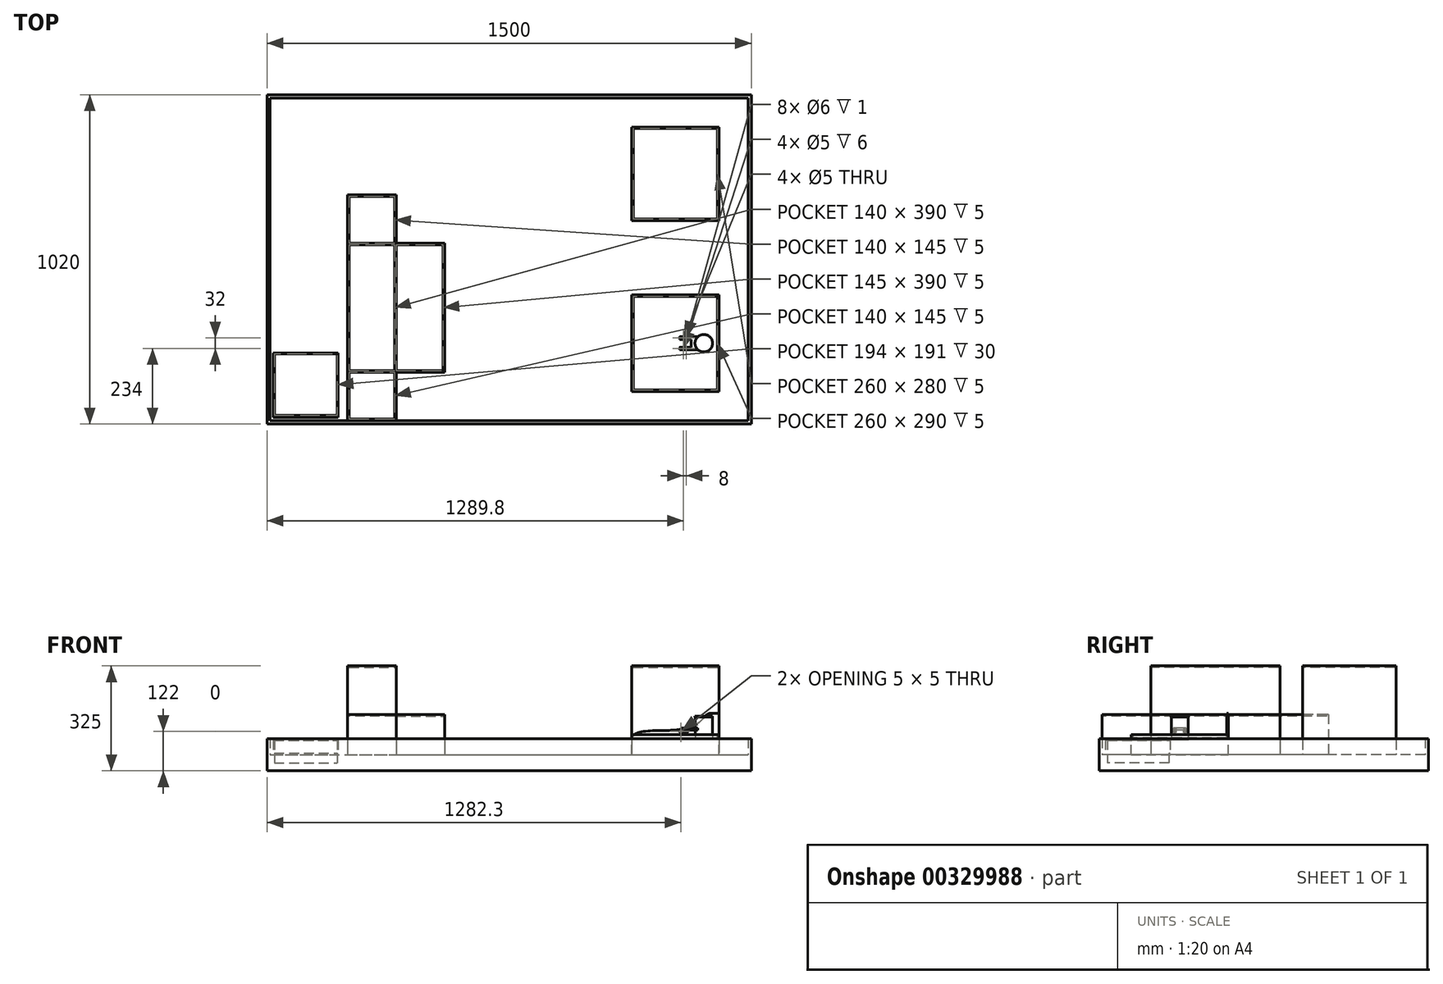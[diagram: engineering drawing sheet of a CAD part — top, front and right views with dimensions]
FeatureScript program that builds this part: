
annotation { "Feature Type Name" : "Feature", "Feature Type Description" : "" }
export const myFeature = defineFeature(function(context is Context, id is Id, definition is map)
    precondition{}
    {
        {
            var Q0;
            Q0=qCreatedBy(makeId("Top.planeOp"),FACE);
            var sketch = newSketch(context, id + "F0", { "sketchPlane" : qUnion([Q0])});
            skCircle(sketch, "E0", {"center": v(0, 0) * mm, "radius": 27.2 * mm});
            skSolve(sketch);
        }
        {
            var Q0;
            Q0=qSketchRegion(id+"F0",true);
            extrude(context, id + "F1", {"entities" : qUnion([Q0]), "depth" : 2.83 * mm});
        }
        {
            var Q0;
            Q0=makeQuery(id+"F1.opExtrude","CAP_FACE",FACE,{"disambiguationData":[OSD([sQuery(id+"F0.wireOp",EDGE,"E0")])],"isStart":false});
            var sketch = newSketch(context, id + "F2", { "sketchPlane" : qUnion([Q0])});
            skCircle(sketch, "E1", {"center": v(0, 0) * mm, "radius": 26.4 * mm});
            skSolve(sketch);
        }
        {
            var Q0;
            Q0=qSketchRegion(id+"F2",true);
            extrude(context, id + "F3", {"entities" : qUnion([Q0]), "operationType" : NewBodyOperationType.ADD, "depth" : 67.36 * mm});
        }
        {
            var Q0;
            Q0=makeQuery(id+"F3.opExtrude","CAP_FACE",FACE,{"disambiguationData":[OSD([sQuery(id+"F2.wireOp",EDGE,"E1")])],"isStart":false});
            var sketch = newSketch(context, id + "F4", { "sketchPlane" : qUnion([Q0])});
            skCircle(sketch, "E2", {"center": v(0, 0) * mm, "radius": 27.2 * mm});
            skSolve(sketch);
        }
        {
            var Q0;
            Q0=qSketchRegion(id+"F4",true);
            extrude(context, id + "F5", {"entities" : qUnion([Q0]), "operationType" : NewBodyOperationType.ADD, "depth" : 2.83 * mm});
        }
        {
            var Q0;
            Q0=makeQuery(id+"F5.opExtrude","CAP_FACE",FACE,{"disambiguationData":[OSD([sQuery(id+"F4.wireOp",EDGE,"E2")])],"isStart":false});
            var sketch = newSketch(context, id + "F6", { "sketchPlane" : qUnion([Q0])});
            skSolve(sketch);
        }
        {
            var Q0;
            Q0=qCreatedBy(makeId("Top.planeOp"),FACE);
            cPlane(context, id + "F7", {"entities" : qUnion([Q0]), "cplaneType" : CPlaneType.OFFSET, "offset" : 25 * mm, "width" : 150 * mm, "height" : 150 * mm});
        }
        {
            var Q0;
            Q0=makeQuery(id+"F6.imprint","IMPRINT",FACE,{"disambiguationData":[TD([[makeQuery(id+"F6.imprint","IMPRINT",EDGE,{"derivedFrom":makeQuery(id+"F5.opExtrude","CAP_EDGE",EDGE,{"disambiguationData":[OSD([sQuery(id+"F4.wireOp",EDGE,"E2")])],"isStart":false})}),1.0]])]});
            var sketch = newSketch(context, id + "F8", { "sketchPlane" : qUnion([Q0])});
            skSolve(sketch);
        }
        {
            var Q0;
            Q0=qCreatedBy(makeId("Top.planeOp"),FACE);
            var sketch = newSketch(context, id + "F9", { "sketchPlane" : qUnion([Q0])});
            skLineSegment(sketch, "E3.bottom", {"start": v(-222.8, -150) * mm, "end": v(47.2, -150) * mm});
            skLineSegment(sketch, "E3.top", {"start": v(-222.8, 150) * mm, "end": v(47.2, 150) * mm});
            skLineSegment(sketch, "E3.left", {"start": v(-222.8, -150) * mm, "end": v(-222.8, 150) * mm});
            skLineSegment(sketch, "E3.right", {"start": v(47.2, -150) * mm, "end": v(47.2, 150) * mm});
            skSolve(sketch);
        }
        {
            var Q0;
            Q0=qSketchRegion(id+"F9",true);
            extrude(context, id + "F10", {"entities" : qUnion([Q0]), "oppositeDirection" : true, "depth" : 72 * mm});
        }
        {
            var Q0;
            Q0=makeQuery(id+"F10.opExtrude","CAP_FACE",FACE,{"disambiguationData":[OSD([sQuery(id+"F9.wireOp",EDGE,"E3.bottom"),sQuery(id+"F9.wireOp",EDGE,"E3.top"),sQuery(id+"F9.wireOp",EDGE,"E3.left"),sQuery(id+"F9.wireOp",EDGE,"E3.right")])],"isStart":true});
            var sketch = newSketch(context, id + "F11", { "sketchPlane" : qUnion([Q0])});
            skLineSegment(sketch, "E4.bottom", {"start": v(-222.8, -150) * mm, "end": v(47.2, -150) * mm});
            skLineSegment(sketch, "E4.top", {"start": v(-222.8, -145) * mm, "end": v(42.2, -145) * mm});
            skLineSegment(sketch, "E4.left", {"start": v(-222.8, -150) * mm, "end": v(-222.8, -145) * mm});
            skLineSegment(sketch, "E5.bottom", {"start": v(47.2, 150) * mm, "end": v(42.2, 150) * mm});
            skLineSegment(sketch, "E5.left", {"start": v(47.2, 150) * mm, "end": v(47.2, -150) * mm});
            skLineSegment(sketch, "E5.right", {"start": v(42.2, 150) * mm, "end": v(42.2, -145) * mm});
            skSolve(sketch);
        }
        {
            var Q0;
            Q0=qSketchRegion(id+"F11",true);
            extrude(context, id + "F12", {"entities" : qUnion([Q0]), "operationType" : NewBodyOperationType.ADD, "depth" : 15 * mm});
        }
        {
            var Q0;
            Q0=makeQuery(id+"F12.boolean.opBoolean","MERGE",FACE,{"derivedFrom":[makeQuery(id+"F10.opExtrude","SWEPT_FACE",FACE,{"disambiguationData":[OSD([sQuery(id+"F9.wireOp",EDGE,"E3.top")])]}),makeQuery(id+"F12.opExtrude","SWEPT_FACE",FACE,{"disambiguationData":[OSD([sQuery(id+"F11.wireOp",EDGE,"E5.bottom")])]})]});
            var sketch = newSketch(context, id + "F13", { "sketchPlane" : qUnion([Q0])});
            skLineSegment(sketch, "E6", {"start": v(-47.2, 81.36) * mm, "end": v(-21.31, 81.36) * mm});
            skFitSpline(sketch, "E7", {"points": [v(-21.31, 81.36) * mm, v(15.24, 52.01) * mm, v(114.14, 28.17) * mm, v(222.8, 0) * mm], "startDerivative": vector(181.02, 0.3) * mm, "endDerivative": vector(-1.73, -239.85) * mm});
            skLineSegment(sketch, "E8", {"start": v(-47.2, 81.36) * mm, "end": v(-47.2, -72) * mm});
            skLineSegment(sketch, "E9", {"start": v(-47.2, -72) * mm, "end": v(222.8, -72) * mm});
            skLineSegment(sketch, "E10", {"start": v(222.8, -72) * mm, "end": v(222.8, 0) * mm});
            skSolve(sketch);
        }
        {
            var Q0;
            Q0=qSketchRegion(id+"F13",true);
            extrude(context, id + "F14", {"entities" : qUnion([Q0]), "operationType" : NewBodyOperationType.ADD, "oppositeDirection" : true, "depth" : 5 * mm});
        }
        {
            var Q0;
            Q0=makeQuery(id+"F10.opExtrude","CAP_FACE",FACE,{"disambiguationData":[OSD([sQuery(id+"F9.wireOp",EDGE,"E3.bottom"),sQuery(id+"F9.wireOp",EDGE,"E3.top"),sQuery(id+"F9.wireOp",EDGE,"E3.left"),sQuery(id+"F9.wireOp",EDGE,"E3.right")])],"isStart":true});
            var sketch = newSketch(context, id + "F15", { "sketchPlane" : qUnion([Q0])});
            skLineSegment(sketch, "E11.bottom", {"start": v(-222.8, 145) * mm, "end": v(-217.8, 145) * mm});
            skLineSegment(sketch, "E11.top", {"start": v(-222.8, -145) * mm, "end": v(-217.8, -145) * mm});
            skLineSegment(sketch, "E11.left", {"start": v(-222.8, 145) * mm, "end": v(-222.8, -145) * mm});
            skLineSegment(sketch, "E11.right", {"start": v(-217.8, 145) * mm, "end": v(-217.8, -145) * mm});
            skSolve(sketch);
        }
        {
            var Q0;
            Q0=qSketchRegion(id+"F15",true);
            extrude(context, id + "F16", {"entities" : qUnion([Q0]), "operationType" : NewBodyOperationType.ADD, "depth" : 5 * mm});
        }
        {
            var Q0;
            Q0=makeQuery(id+"F10.opExtrude","CAP_FACE",FACE,{"disambiguationData":[OSD([sQuery(id+"F9.wireOp",EDGE,"E3.bottom"),sQuery(id+"F9.wireOp",EDGE,"E3.top"),sQuery(id+"F9.wireOp",EDGE,"E3.left"),sQuery(id+"F9.wireOp",EDGE,"E3.right")])],"isStart":false});
            var sketch = newSketch(context, id + "F17", { "sketchPlane" : qUnion([Q0])});
            skLineSegment(sketch, "E12.bottom", {"start": v(147.2, 250) * mm, "end": v(-1352.8, 250) * mm});
            skLineSegment(sketch, "E12.top", {"start": v(147.2, -770) * mm, "end": v(-1352.8, -770) * mm});
            skLineSegment(sketch, "E12.left", {"start": v(147.2, 250) * mm, "end": v(147.2, -770) * mm});
            skLineSegment(sketch, "E12.right", {"start": v(-1352.8, 250) * mm, "end": v(-1352.8, -770) * mm});
            skSolve(sketch);
        }
        {
            var Q0;
            Q0=qSketchRegion(id+"F17",true);
            extrude(context, id + "F18", {"entities" : qUnion([Q0]), "operationType" : NewBodyOperationType.ADD, "depth" : 25 * mm});
        }
        {
            var Q0;
            Q0=makeQuery(id+"F18.opExtrude","CAP_FACE",FACE,{"disambiguationData":[OSD([sQuery(id+"F17.wireOp",EDGE,"E12.bottom"),sQuery(id+"F17.wireOp",EDGE,"E12.top"),sQuery(id+"F17.wireOp",EDGE,"E12.left"),sQuery(id+"F17.wireOp",EDGE,"E12.right")])],"isStart":true});
            var sketch = newSketch(context, id + "F19", { "sketchPlane" : qUnion([Q0])});
            skLineSegment(sketch, "E13.bottom", {"start": v(-222.8, 670) * mm, "end": v(47.2, 670) * mm});
            skLineSegment(sketch, "E13.top", {"start": v(-222.8, 380) * mm, "end": v(47.2, 380) * mm});
            skLineSegment(sketch, "E13.left", {"start": v(-222.8, 670) * mm, "end": v(-222.8, 380) * mm});
            skLineSegment(sketch, "E13.right", {"start": v(47.2, 670) * mm, "end": v(47.2, 380) * mm});
            skSolve(sketch);
        }
        {
            var Q0;
            Q0=qSketchRegion(id+"F19",true);
            extrude(context, id + "F20", {"entities" : qUnion([Q0]), "operationType" : NewBodyOperationType.ADD, "depth" : 300 * mm});
        }
        {
            var Q0;
            Q0=makeQuery(id+"F20.opExtrude","CAP_FACE",FACE,{"disambiguationData":[OSD([sQuery(id+"F19.wireOp",EDGE,"E13.bottom"),sQuery(id+"F19.wireOp",EDGE,"E13.top"),sQuery(id+"F19.wireOp",EDGE,"E13.left"),sQuery(id+"F19.wireOp",EDGE,"E13.right")])],"isStart":false});
            var sketch = newSketch(context, id + "F21", { "sketchPlane" : qUnion([Q0])});
            skLineSegment(sketch, "E14.bottom", {"start": v(-217.8, 665) * mm, "end": v(42.2, 665) * mm});
            skLineSegment(sketch, "E14.top", {"start": v(-217.8, 385) * mm, "end": v(42.2, 385) * mm});
            skLineSegment(sketch, "E14.left", {"start": v(-217.8, 665) * mm, "end": v(-217.8, 385) * mm});
            skLineSegment(sketch, "E14.right", {"start": v(42.2, 665) * mm, "end": v(42.2, 385) * mm});
            skSolve(sketch);
        }
        {
            var Q0;
            Q0=qSketchRegion(id+"F21",true);
            extrude(context, id + "F22", {"entities" : qUnion([Q0]), "operationType" : NewBodyOperationType.REMOVE, "oppositeDirection" : true, "depth" : 5 * mm});
        }
        {
            var Q0;
            Q0=makeQuery(id+"F18.opExtrude","CAP_FACE",FACE,{"disambiguationData":[OSD([sQuery(id+"F17.wireOp",EDGE,"E12.bottom"),sQuery(id+"F17.wireOp",EDGE,"E12.top"),sQuery(id+"F17.wireOp",EDGE,"E12.left"),sQuery(id+"F17.wireOp",EDGE,"E12.right")])],"isStart":true});
            var sketch = newSketch(context, id + "F23", { "sketchPlane" : qUnion([Q0])});
            skLineSegment(sketch, "E15.bottom", {"start": v(-1352.8, 770) * mm, "end": v(147.2, 770) * mm});
            skLineSegment(sketch, "E15.top", {"start": v(-1352.8, -250) * mm, "end": v(147.2, -250) * mm});
            skLineSegment(sketch, "E15.left", {"start": v(-1352.8, 770) * mm, "end": v(-1352.8, -250) * mm});
            skLineSegment(sketch, "E15.right", {"start": v(147.2, 770) * mm, "end": v(147.2, -250) * mm});
            skLineSegment(sketch, "E16.bottom", {"start": v(-1342.8, 760) * mm, "end": v(137.2, 760) * mm});
            skLineSegment(sketch, "E16.top", {"start": v(-1342.8, -240) * mm, "end": v(137.2, -240) * mm});
            skLineSegment(sketch, "E16.left", {"start": v(-1342.8, 760) * mm, "end": v(-1342.8, -240) * mm});
            skLineSegment(sketch, "E16.right", {"start": v(137.2, 760) * mm, "end": v(137.2, -240) * mm});
            skSolve(sketch);
        }
        {
            var Q0;
            Q0=qSketchRegion(id+"F23",true);
            extrude(context, id + "F24", {"entities" : qUnion([Q0]), "operationType" : NewBodyOperationType.ADD, "depth" : 75 * mm});
        }
        {
            var Q0;
            Q0=makeQuery(id+"F18.opExtrude","CAP_FACE",FACE,{"disambiguationData":[OSD([sQuery(id+"F17.wireOp",EDGE,"E12.bottom"),sQuery(id+"F17.wireOp",EDGE,"E12.top"),sQuery(id+"F17.wireOp",EDGE,"E12.left"),sQuery(id+"F17.wireOp",EDGE,"E12.right")])],"isStart":true});
            var sketch = newSketch(context, id + "F25", { "sketchPlane" : qUnion([Q0])});
            skLineSegment(sketch, "E17.bottom", {"start": v(-1102.8, 460) * mm, "end": v(-952.8, 460) * mm});
            skLineSegment(sketch, "E17.top", {"start": v(-1102.8, -240) * mm, "end": v(-952.8, -240) * mm});
            skLineSegment(sketch, "E17.left", {"start": v(-1102.8, 460) * mm, "end": v(-1102.8, -240) * mm});
            skLineSegment(sketch, "E17.right", {"start": v(-952.8, 460) * mm, "end": v(-952.8, 310) * mm});
            skLineSegment(sketch, "E18.bottom", {"start": v(-952.8, 310) * mm, "end": v(-802.8, 310) * mm});
            skLineSegment(sketch, "E18.top", {"start": v(-952.8, -90) * mm, "end": v(-802.8, -90) * mm});
            skLineSegment(sketch, "E18.right", {"start": v(-802.8, 310) * mm, "end": v(-802.8, -90) * mm});
            skLineSegment(sketch, "E19.trimOffspring", {"start": v(-952.8, -90) * mm, "end": v(-952.8, -240) * mm});
            skSolve(sketch);
        }
        {
            var Q0;
            Q0=qSketchRegion(id+"F25",true);
            extrude(context, id + "F26", {"entities" : qUnion([Q0]), "operationType" : NewBodyOperationType.ADD, "depth" : 150 * mm});
        }
        {
            var Q0;
            Q0=makeQuery(id+"F26.opExtrude","CAP_FACE",FACE,{"disambiguationData":[OSD([sQuery(id+"F25.wireOp",EDGE,"E17.bottom"),sQuery(id+"F25.wireOp",EDGE,"E17.top"),sQuery(id+"F25.wireOp",EDGE,"E17.left"),sQuery(id+"F25.wireOp",EDGE,"E17.right"),sQuery(id+"F25.wireOp",EDGE,"E18.bottom"),sQuery(id+"F25.wireOp",EDGE,"E18.top"),sQuery(id+"F25.wireOp",EDGE,"E18.right"),sQuery(id+"F25.wireOp",EDGE,"E19.trimOffspring")])],"isStart":false});
            var sketch = newSketch(context, id + "F27", { "sketchPlane" : qUnion([Q0])});
            skLineSegment(sketch, "E20.bottom", {"start": v(-952.8, 310) * mm, "end": v(-1102.8, 310) * mm});
            skLineSegment(sketch, "E20.top", {"start": v(-952.8, -90) * mm, "end": v(-1102.8, -90) * mm});
            skLineSegment(sketch, "E20.left", {"start": v(-952.8, 310) * mm, "end": v(-952.8, -90) * mm});
            skLineSegment(sketch, "E20.right", {"start": v(-1102.8, 310) * mm, "end": v(-1102.8, -90) * mm});
            skSolve(sketch);
        }
        {
            var Q0;
            Q0=qSketchRegion(id+"F27",true);
            extrude(context, id + "F28", {"entities" : qUnion([Q0]), "operationType" : NewBodyOperationType.ADD, "depth" : 150 * mm});
        }
        {
            var Q0;
            Q0=makeQuery(id+"F28.opExtrude","CAP_FACE",FACE,{"disambiguationData":[OSD([sQuery(id+"F27.wireOp",EDGE,"E20.bottom"),sQuery(id+"F27.wireOp",EDGE,"E20.top"),sQuery(id+"F27.wireOp",EDGE,"E20.left"),sQuery(id+"F27.wireOp",EDGE,"E20.right")])],"isStart":false});
            var sketch = newSketch(context, id + "F29", { "sketchPlane" : qUnion([Q0])});
            skLineSegment(sketch, "E21.bottom", {"start": v(-1097.8, 305) * mm, "end": v(-957.8, 305) * mm});
            skLineSegment(sketch, "E21.top", {"start": v(-1097.8, -85) * mm, "end": v(-957.8, -85) * mm});
            skLineSegment(sketch, "E21.left", {"start": v(-1097.8, 305) * mm, "end": v(-1097.8, -85) * mm});
            skLineSegment(sketch, "E21.right", {"start": v(-957.8, 305) * mm, "end": v(-957.8, -85) * mm});
            skSolve(sketch);
        }
        {
            var Q0;
            Q0=qSketchRegion(id+"F29",true);
            extrude(context, id + "F30", {"entities" : qUnion([Q0]), "operationType" : NewBodyOperationType.REMOVE, "oppositeDirection" : true, "depth" : 5 * mm});
        }
        {
            var Q0;
            {var subQ0=sQuery(id+"F25.wireOp",EDGE,"E17.left");var subQ1=sQuery(id+"F25.wireOp",EDGE,"E18.bottom");var subQ2=sQuery(id+"F25.wireOp",EDGE,"E17.right");var subQ3=sQuery(id+"F25.wireOp",EDGE,"E17.bottom");var subQ4=makeQuery(id+"F26.opExtrude","CAP_FACE",FACE,{"disambiguationData":[OSD([subQ3,sQuery(id+"F25.wireOp",EDGE,"E17.top"),subQ0,subQ2,subQ1,sQuery(id+"F25.wireOp",EDGE,"E18.top"),sQuery(id+"F25.wireOp",EDGE,"E18.right"),sQuery(id+"F25.wireOp",EDGE,"E19.trimOffspring")])],"isStart":false});Q0=makeQuery(id+"F28.boolean.opBoolean","SPLIT",FACE,{"disambiguationData":[TD([makeQuery(id+"F26.opExtrude","SWEPT_FACE",FACE,{"disambiguationData":[OSD([subQ3])]})])],"derivedFrom":subQ4});}
            var sketch = newSketch(context, id + "F31", { "sketchPlane" : qUnion([Q0])});
            skLineSegment(sketch, "E22.bottom", {"start": v(-1097.8, 455) * mm, "end": v(-957.8, 455) * mm});
            skLineSegment(sketch, "E22.top", {"start": v(-1097.8, 310) * mm, "end": v(-957.8, 310) * mm});
            skLineSegment(sketch, "E22.left", {"start": v(-1097.8, 455) * mm, "end": v(-1097.8, 310) * mm});
            skLineSegment(sketch, "E22.right", {"start": v(-957.8, 455) * mm, "end": v(-957.8, 310) * mm});
            skLineSegment(sketch, "E23.bottom", {"start": v(-952.8, 305) * mm, "end": v(-807.8, 305) * mm});
            skLineSegment(sketch, "E23.top", {"start": v(-952.8, -85) * mm, "end": v(-807.8, -85) * mm});
            skLineSegment(sketch, "E23.left", {"start": v(-952.8, 305) * mm, "end": v(-952.8, -85) * mm});
            skLineSegment(sketch, "E23.right", {"start": v(-807.8, 305) * mm, "end": v(-807.8, -85) * mm});
            skLineSegment(sketch, "E24.bottom", {"start": v(-1097.8, -90) * mm, "end": v(-957.8, -90) * mm});
            skLineSegment(sketch, "E24.top", {"start": v(-1097.8, -235) * mm, "end": v(-957.8, -235) * mm});
            skLineSegment(sketch, "E24.left", {"start": v(-1097.8, -90) * mm, "end": v(-1097.8, -235) * mm});
            skLineSegment(sketch, "E24.right", {"start": v(-957.8, -90) * mm, "end": v(-957.8, -235) * mm});
            skSolve(sketch);
        }
        {
            var Q0;
            Q0=qSketchRegion(id+"F31",true);
            extrude(context, id + "F32", {"entities" : qUnion([Q0]), "operationType" : NewBodyOperationType.REMOVE, "oppositeDirection" : true, "depth" : 5 * mm});
        }
        {
            var Q0;
            Q0=qCreatedBy(id+"F7.planeOp",FACE);
            var sketch = newSketch(context, id + "F33", { "sketchPlane" : qUnion([Q0])});
            skLineSegment(sketch, "E25", {"start": v(0, 0) * mm, "end": v(-90, 0) * mm, "construction": true});
            skLineSegment(sketch, "E26.bottom", {"start": v(-74.5, -12) * mm, "end": v(-55, -12) * mm});
            skLineSegment(sketch, "E26.top", {"start": v(-74.5, -20) * mm, "end": v(-55, -20) * mm});
            skLineSegment(sketch, "E26.left", {"start": v(-74.5, -12) * mm, "end": v(-74.5, -13) * mm});
            skPoint(sketch, "E27.visualSharp", {"position": v(-51, -12) * mm});
            skPoint(sketch, "E28.visualSharp", {"position": v(-51, -20) * mm});
            skCircle(sketch, "E29", {"center": v(-55, -16) * mm, "radius": 3 * mm});
            skLineSegment(sketch, "E30", {"start": v(-59, -3.98) * mm, "end": v(-59, -18.08) * mm, "construction": true});
            skCircle(sketch, "E31.MirrorC", {"center": v(-63, -16) * mm, "radius": 3 * mm});
            skLineSegment(sketch, "E32.bottom", {"start": v(-74.5, -13) * mm, "end": v(-65.65, -13) * mm});
            skLineSegment(sketch, "E32.top", {"start": v(-74.5, -19) * mm, "end": v(-65.65, -19) * mm});
            skArc(sketch, "E33", {"start": v(-65.65, -13) * mm, "mid": v(-67, -16) * mm, "end": v(-65.65, -19) * mm});
            skLineSegment(sketch, "E34.trimOffspring", {"start": v(-74.5, -19) * mm, "end": v(-74.5, -20) * mm});
            skArc(sketch, "E35.trimOffspring", {"start": v(-55, -20) * mm, "mid": v(-51, -16) * mm, "end": v(-55, -12) * mm});
            skLineSegment(sketch, "E36.MirrorCS", {"start": v(-74.5, 12) * mm, "end": v(-74.5, 13) * mm});
            skLineSegment(sketch, "E37.MirrorCS", {"start": v(-74.5, 19) * mm, "end": v(-74.5, 20) * mm});
            skPoint(sketch, "E38.MirrorP", {"position": v(-51, 12) * mm});
            skLineSegment(sketch, "E39.MirrorCS", {"start": v(-74.5, 12) * mm, "end": v(-55, 12) * mm});
            skPoint(sketch, "E40.MirrorP", {"position": v(-51, 20) * mm});
            skArc(sketch, "E41.MirrorCS", {"start": v(-65.65, 13) * mm, "mid": v(-67, 16) * mm, "end": v(-65.65, 19) * mm});
            skArc(sketch, "E42.MirrorCS", {"start": v(-55, 20) * mm, "mid": v(-51, 16) * mm, "end": v(-55, 12) * mm});
            skLineSegment(sketch, "E43.MirrorCS", {"start": v(-74.5, 20) * mm, "end": v(-55, 20) * mm});
            skCircle(sketch, "E44.MirrorC", {"center": v(-55, 16) * mm, "radius": 3 * mm});
            skCircle(sketch, "E45.MirrorC", {"center": v(-63, 16) * mm, "radius": 3 * mm});
            skLineSegment(sketch, "E46.MirrorCS", {"start": v(-74.5, 19) * mm, "end": v(-65.65, 19) * mm});
            skLineSegment(sketch, "E47.MirrorCS", {"start": v(-74.5, 13) * mm, "end": v(-65.65, 13) * mm});
            skSolve(sketch);
        }
        {
            var Q0;
            Q0=qSketchRegion(id+"F33",true);
            var Q1;
            Q1=qSketchRegion(id+"F36",true);
            extrude(context, id + "F34", {"entities" : qUnion([Q0, Q1]), "endBound" : BoundingType.SYMMETRIC, "depth" : 8 * mm});
        }
        {
            var Q0;
            Q0=makeQuery(id+"F34.opExtrude","CAP_EDGE",EDGE,{"disambiguationData":[OSD([sQuery(id+"F33.wireOp",EDGE,"E34.trimOffspring")])],"isStart":false});
            var Q1;
            Q1=makeQuery(id+"F34.opExtrude","CAP_EDGE",EDGE,{"disambiguationData":[OSD([sQuery(id+"F33.wireOp",EDGE,"E26.left")])],"isStart":false});
            var Q2;
            Q2=makeQuery(id+"F34.opExtrude","CAP_EDGE",EDGE,{"disambiguationData":[OSD([sQuery(id+"F33.wireOp",EDGE,"E34.trimOffspring")])],"isStart":true});
            var Q3;
            Q3=makeQuery(id+"F34.opExtrude","CAP_EDGE",EDGE,{"disambiguationData":[OSD([sQuery(id+"F33.wireOp",EDGE,"E26.left")])],"isStart":true});
            var Q4;
            Q4=makeQuery(id+"F34.opExtrude","CAP_EDGE",EDGE,{"disambiguationData":[OSD([sQuery(id+"F33.wireOp",EDGE,"E36.MirrorCS")])],"isStart":false});
            var Q5;
            Q5=makeQuery(id+"F34.opExtrude","CAP_EDGE",EDGE,{"disambiguationData":[OSD([sQuery(id+"F33.wireOp",EDGE,"E37.MirrorCS")])],"isStart":false});
            var Q6;
            Q6=makeQuery(id+"F34.opExtrude","CAP_EDGE",EDGE,{"disambiguationData":[OSD([sQuery(id+"F33.wireOp",EDGE,"E37.MirrorCS")])],"isStart":true});
            var Q7;
            Q7=makeQuery(id+"F34.opExtrude","CAP_EDGE",EDGE,{"disambiguationData":[OSD([sQuery(id+"F33.wireOp",EDGE,"E36.MirrorCS")])],"isStart":true});
            fillet(context, id + "F35", {"entities" : qUnion([Q0, Q1, Q2, Q3, Q4, Q5, Q6, Q7]), "radius" : 4 * mm, "tangentPropagation" : true, "allowEdgeOverflow" : false});
        }
        {
            var Q0;
            Q0=makeQuery(id+"F34.opExtrude","SWEPT_FACE",FACE,{"disambiguationData":[OSD([sQuery(id+"F33.wireOp",EDGE,"E26.top")])]});
            var sketch = newSketch(context, id + "F36", { "sketchPlane" : qUnion([Q0])});
            skCircle(sketch, "E48", {"center": v(-70.5, 25) * mm, "radius": 3 * mm});
            skSolve(sketch);
        }
        {
            var Q0;
            Q0=qSketchRegion(id+"F36",true);
            var Q1;
            Q1=makeQuery(id+"F34.opExtrude","SWEPT_FACE",FACE,{"disambiguationData":[OSD([sQuery(id+"F33.wireOp",EDGE,"E26.bottom")])]});
            extrude(context, id + "F37", {"entities" : qUnion([Q0]), "operationType" : NewBodyOperationType.ADD, "endBound" : BoundingType.UP_TO_SURFACE, "oppositeDirection" : true, "endBoundEntityFace" : qUnion([Q1]), "depth" : 25 * mm});
        }
        {
            var Q0;
            Q0=makeQuery(id+"F34.opExtrude","SWEPT_FACE",FACE,{"disambiguationData":[OSD([sQuery(id+"F33.wireOp",EDGE,"E43.MirrorCS")])]});
            var sketch = newSketch(context, id + "F38", { "sketchPlane" : qUnion([Q0])});
            skCircle(sketch, "E49", {"center": v(70.5, 25) * mm, "radius": 3 * mm});
            skSolve(sketch);
        }
        {
            var Q0;
            Q0=qSketchRegion(id+"F38",true);
            var Q1;
            Q1=makeQuery(id+"F34.opExtrude","SWEPT_FACE",FACE,{"disambiguationData":[OSD([sQuery(id+"F33.wireOp",EDGE,"E39.MirrorCS")])]});
            extrude(context, id + "F39", {"entities" : qUnion([Q0]), "operationType" : NewBodyOperationType.ADD, "endBound" : BoundingType.UP_TO_SURFACE, "oppositeDirection" : true, "endBoundEntityFace" : qUnion([Q1]), "depth" : 25 * mm});
        }
        {
            var Q0;
            Q0=qCreatedBy(id+"F7.planeOp",FACE);
            var sketch = newSketch(context, id + "F40", { "sketchPlane" : qUnion([Q0])});
            skCircle(sketch, "E50", {"center": v(-55, 16) * mm, "radius": 3 * mm});
            skCircle(sketch, "E51", {"center": v(-63, 16) * mm, "radius": 2.5 * mm});
            skCircle(sketch, "E52", {"center": v(-63, 16) * mm, "radius": 3 * mm});
            skCircle(sketch, "E53", {"center": v(-55, 16) * mm, "radius": 2.5 * mm});
            skSolve(sketch);
        }
        {
            var Q0;
            Q0=qSketchRegion(id+"F40",true);
            extrude(context, id + "F41", {"entities" : qUnion([Q0]), "operationType" : NewBodyOperationType.ADD, "endBound" : BoundingType.SYMMETRIC, "depth" : 6 * mm});
        }
        {
            var Q0;
            Q0=qCreatedBy(id+"F7.planeOp",FACE);
            var sketch = newSketch(context, id + "F42", { "sketchPlane" : qUnion([Q0])});
            skCircle(sketch, "E54", {"center": v(-63, -16) * mm, "radius": 2.5 * mm});
            skCircle(sketch, "E55", {"center": v(-63, -16) * mm, "radius": 3 * mm});
            skCircle(sketch, "E56", {"center": v(-55, -16) * mm, "radius": 2.5 * mm});
            skCircle(sketch, "E57", {"center": v(-55, -16) * mm, "radius": 3 * mm});
            skSolve(sketch);
        }
        {
            var Q0;
            Q0=qSketchRegion(id+"F42",true);
            extrude(context, id + "F43", {"entities" : qUnion([Q0]), "operationType" : NewBodyOperationType.ADD, "endBound" : BoundingType.SYMMETRIC, "depth" : 6 * mm});
        }
        {
            var Q0;
            Q0=makeQuery(id+"F34.opExtrude","SWEPT_FACE",FACE,{"disambiguationData":[OSD([sQuery(id+"F33.wireOp",EDGE,"E43.MirrorCS")])]});
            var sketch = newSketch(context, id + "F44", { "sketchPlane" : qUnion([Q0])});
            skArc(sketch, "E58", {"start": v(71.5, 27.3) * mm, "mid": v(70.5, 27.5) * mm, "end": v(69.5, 27.3) * mm});
            skLineSegment(sketch, "E59.bottom", {"start": v(68.2, 26) * mm, "end": v(69.5, 26) * mm});
            skLineSegment(sketch, "E59.top", {"start": v(68.2, 24) * mm, "end": v(69.5, 24) * mm});
            skLineSegment(sketch, "E60.left", {"start": v(71.5, 27.3) * mm, "end": v(71.5, 26) * mm});
            skLineSegment(sketch, "E60.right", {"start": v(69.5, 27.3) * mm, "end": v(69.5, 26) * mm});
            skPoint(sketch, "E61.orphan", {"position": v(69.5, 27.8) * mm});
            skPoint(sketch, "E62.orphan", {"position": v(71.5, 27.8) * mm});
            skArc(sketch, "E63.trimOffspring", {"start": v(68.2, 26) * mm, "mid": v(68, 25) * mm, "end": v(68.2, 24) * mm});
            skPoint(sketch, "E59.left.start.orphan", {"position": v(67.32, 26) * mm});
            skPoint(sketch, "E64.orphan", {"position": v(67.32, 24) * mm});
            skArc(sketch, "E65.trimOffspring", {"start": v(69.5, 22.7) * mm, "mid": v(70.5, 22.5) * mm, "end": v(71.5, 22.7) * mm});
            skLineSegment(sketch, "E66.trimOffspring", {"start": v(69.5, 24) * mm, "end": v(69.5, 22.7) * mm});
            skLineSegment(sketch, "E67.trimOffspring", {"start": v(71.5, 26) * mm, "end": v(72.8, 26) * mm});
            skLineSegment(sketch, "E68.trimOffspring", {"start": v(71.5, 24) * mm, "end": v(71.5, 22.7) * mm});
            skLineSegment(sketch, "E69.trimOffspring", {"start": v(71.5, 24) * mm, "end": v(72.8, 24) * mm});
            skPoint(sketch, "E60.top.end.orphan", {"position": v(69.5, 22.2) * mm});
            skPoint(sketch, "E70.orphan", {"position": v(71.5, 22.2) * mm});
            skPoint(sketch, "E59.right.end.orphan", {"position": v(73.68, 24) * mm});
            skPoint(sketch, "E71.orphan", {"position": v(73.68, 26) * mm});
            skArc(sketch, "E72.trimOffspring", {"start": v(72.8, 24) * mm, "mid": v(73, 25) * mm, "end": v(72.8, 26) * mm});
            skSolve(sketch);
        }
        {
            var Q0;
            Q0=qSketchRegion(id+"F44",true);
            extrude(context, id + "F45", {"entities" : qUnion([Q0]), "operationType" : NewBodyOperationType.REMOVE, "endBound" : BoundingType.THROUGH_ALL, "oppositeDirection" : true, "depth" : 25 * mm});
        }
        {
            var Q0;
            Q0=makeQuery(id+"F18.opExtrude","CAP_FACE",FACE,{"disambiguationData":[OSD([sQuery(id+"F17.wireOp",EDGE,"E12.bottom"),sQuery(id+"F17.wireOp",EDGE,"E12.top"),sQuery(id+"F17.wireOp",EDGE,"E12.left"),sQuery(id+"F17.wireOp",EDGE,"E12.right")])],"isStart":true});
            var sketch = newSketch(context, id + "F46", { "sketchPlane" : qUnion([Q0])});
            skLineSegment(sketch, "E73.bottom", {"start": v(-1332.8, -30) * mm, "end": v(-1132.8, -30) * mm});
            skLineSegment(sketch, "E73.top", {"start": v(-1332.8, -230) * mm, "end": v(-1132.8, -230) * mm});
            skLineSegment(sketch, "E73.left", {"start": v(-1332.8, -30) * mm, "end": v(-1332.8, -230) * mm});
            skLineSegment(sketch, "E73.right", {"start": v(-1132.8, -30) * mm, "end": v(-1132.8, -230) * mm});
            skLineSegment(sketch, "E74.bottom", {"start": v(-1329.8, -33) * mm, "end": v(-1135.8, -33) * mm});
            skLineSegment(sketch, "E74.top", {"start": v(-1329.8, -224) * mm, "end": v(-1135.8, -224) * mm});
            skLineSegment(sketch, "E74.left", {"start": v(-1329.8, -33) * mm, "end": v(-1329.8, -224) * mm});
            skLineSegment(sketch, "E74.right", {"start": v(-1135.8, -33) * mm, "end": v(-1135.8, -224) * mm});
            skSolve(sketch);
        }
        {
            var Q0;
            Q0=qSketchRegion(id+"F46",true);
            extrude(context, id + "F47", {"entities" : qUnion([Q0]), "operationType" : NewBodyOperationType.ADD, "depth" : 30 * mm});
        }
        {
            var Q0;
            Q0=makeQuery(id+"F47.opExtrude","CAP_FACE",FACE,{"disambiguationData":[OSD([sQuery(id+"F46.wireOp",EDGE,"E73.bottom"),sQuery(id+"F46.wireOp",EDGE,"E73.top"),sQuery(id+"F46.wireOp",EDGE,"E73.left"),sQuery(id+"F46.wireOp",EDGE,"E73.right"),sQuery(id+"F46.wireOp",EDGE,"E74.bottom"),sQuery(id+"F46.wireOp",EDGE,"E74.top"),sQuery(id+"F46.wireOp",EDGE,"E74.left"),sQuery(id+"F46.wireOp",EDGE,"E74.right")])],"isStart":false});
            var sketch = newSketch(context, id + "F48", { "sketchPlane" : qUnion([Q0])});
            skLineSegment(sketch, "E75.bottom", {"start": v(-1332.8, -30) * mm, "end": v(-1329.8, -30) * mm});
            skLineSegment(sketch, "E75.top", {"start": v(-1332.8, -230) * mm, "end": v(-1329.8, -230) * mm});
            skLineSegment(sketch, "E75.left", {"start": v(-1332.8, -30) * mm, "end": v(-1332.8, -230) * mm});
            skLineSegment(sketch, "E75.right", {"start": v(-1329.8, -30) * mm, "end": v(-1329.8, -224) * mm});
            skLineSegment(sketch, "E76.bottom", {"start": v(-1329.8, -230) * mm, "end": v(-1135.8, -230) * mm});
            skLineSegment(sketch, "E76.top", {"start": v(-1329.8, -224) * mm, "end": v(-1135.8, -224) * mm});
            skLineSegment(sketch, "E77.bottom", {"start": v(-1135.8, -230) * mm, "end": v(-1132.8, -230) * mm});
            skLineSegment(sketch, "E77.top", {"start": v(-1135.8, -30) * mm, "end": v(-1132.8, -30) * mm});
            skLineSegment(sketch, "E77.left", {"start": v(-1135.8, -224) * mm, "end": v(-1135.8, -30) * mm});
            skLineSegment(sketch, "E77.right", {"start": v(-1132.8, -230) * mm, "end": v(-1132.8, -30) * mm});
            skSolve(sketch);
        }
        {
            var Q0;
            Q0=qSketchRegion(id+"F48",true);
            extrude(context, id + "F49", {"entities" : qUnion([Q0]), "operationType" : NewBodyOperationType.ADD, "depth" : 40 * mm});
        }
        {
            var Q0;
            Q0=makeQuery(id+"F34.opExtrude","CAP_FACE",FACE,{"disambiguationData":[OSD([sQuery(id+"F33.wireOp",EDGE,"E36.MirrorCS"),sQuery(id+"F33.wireOp",EDGE,"E37.MirrorCS"),sQuery(id+"F33.wireOp",EDGE,"E39.MirrorCS"),sQuery(id+"F33.wireOp",EDGE,"E41.MirrorCS"),sQuery(id+"F33.wireOp",EDGE,"E42.MirrorCS"),sQuery(id+"F33.wireOp",EDGE,"E43.MirrorCS"),sQuery(id+"F33.wireOp",EDGE,"E44.MirrorC"),sQuery(id+"F33.wireOp",EDGE,"E45.MirrorC"),sQuery(id+"F33.wireOp",EDGE,"E46.MirrorCS"),sQuery(id+"F33.wireOp",EDGE,"E47.MirrorCS")])],"isStart":false});
            var sketch = newSketch(context, id + "F50", { "sketchPlane" : qUnion([Q0])});
            skLineSegment(sketch, "E78", {"start": v(-18.43, 20) * mm, "end": v(-17.96, 20) * mm});
            skPoint(sketch, "E78.startSnap0", {"position": v(-68.07, 19) * mm});
            skArc(sketch, "E79", {"start": v(-18.43, 20) * mm, "mid": v(-27.2, 0) * mm, "end": v(-18.43, -20) * mm});
            skLineSegment(sketch, "E80", {"start": v(-70.5, -20) * mm, "end": v(-18.43, -20) * mm});
            skLineSegment(sketch, "E81", {"start": v(-38.9, 12) * mm, "end": v(-38.9, -12) * mm});
            skLineSegment(sketch, "E82", {"start": v(-70.5, -20) * mm, "end": v(-70.5, -12) * mm});
            skPoint(sketch, "E83.orphan", {"position": v(-68.07, 20) * mm});
            skLineSegment(sketch, "E84", {"start": v(-70.5, 20) * mm, "end": v(-17.96, 20) * mm});
            skLineSegment(sketch, "E85", {"start": v(-38.9, 12) * mm, "end": v(-70.5, 12) * mm});
            skCircle(sketch, "E86", {"center": v(-63, -16) * mm, "radius": 2.5 * mm});
            skCircle(sketch, "E87", {"center": v(-55, -16) * mm, "radius": 2.5 * mm});
            skCircle(sketch, "E88", {"center": v(-63, 16) * mm, "radius": 2.5 * mm});
            skCircle(sketch, "E89", {"center": v(-55, 16) * mm, "radius": 2.5 * mm});
            skLineSegment(sketch, "E90", {"start": v(-70.5, -12) * mm, "end": v(-38.9, -12) * mm});
            skLineSegment(sketch, "E91.trimOffspring", {"start": v(-70.5, 12) * mm, "end": v(-70.5, 20) * mm});
            skArc(sketch, "E92", {"start": v(0.4, -27.17) * mm, "mid": v(19.04, 19.36) * mm, "end": v(-27.2, 0) * mm});
            skSolve(sketch);
        }
        {
            var Q0;
            Q0=makeQuery(id+"F46.imprint","IMPRINT",FACE,{"disambiguationData":[TD([[makeQuery(id+"F46.imprint","IMPRINT",EDGE,{"derivedFrom":sQuery(id+"F46.wireOp",EDGE,"E73.bottom")}),1.0]])]});
            var Q1;
            Q1=makeQuery(id+"F47.boolean.opBoolean","SPLIT",FACE,{"disambiguationData":[TD([makeQuery(id+"F10.opExtrude","SWEPT_FACE",FACE,{"disambiguationData":[OSD([sQuery(id+"F9.wireOp",EDGE,"E3.bottom")])]})])],"derivedFrom":makeQuery(id+"F18.opExtrude","CAP_FACE",FACE,{"disambiguationData":[OSD([sQuery(id+"F17.wireOp",EDGE,"E12.bottom"),sQuery(id+"F17.wireOp",EDGE,"E12.top"),sQuery(id+"F17.wireOp",EDGE,"E12.left"),sQuery(id+"F17.wireOp",EDGE,"E12.right")])],"isStart":true})});
            var Q2;
            Q2=makeQuery(id+"F18.opExtrude","CAP_FACE",FACE,{"disambiguationData":[OSD([sQuery(id+"F17.wireOp",EDGE,"E12.bottom"),sQuery(id+"F17.wireOp",EDGE,"E12.top"),sQuery(id+"F17.wireOp",EDGE,"E12.left"),sQuery(id+"F17.wireOp",EDGE,"E12.right")])],"isStart":false});
            extrude(context, id + "F51", {"entities" : qUnion([Q0, Q1, Q2]), "operationType" : NewBodyOperationType.ADD, "depth" : 25 * mm});
        }
        {
            var Q0;
            Q0 = qSketchRegion(id + "F50", true);
            extrude(context, id + "F52", {"entities" : qUnion([Q0]), "depth" : 6 * mm});
        }
    });
